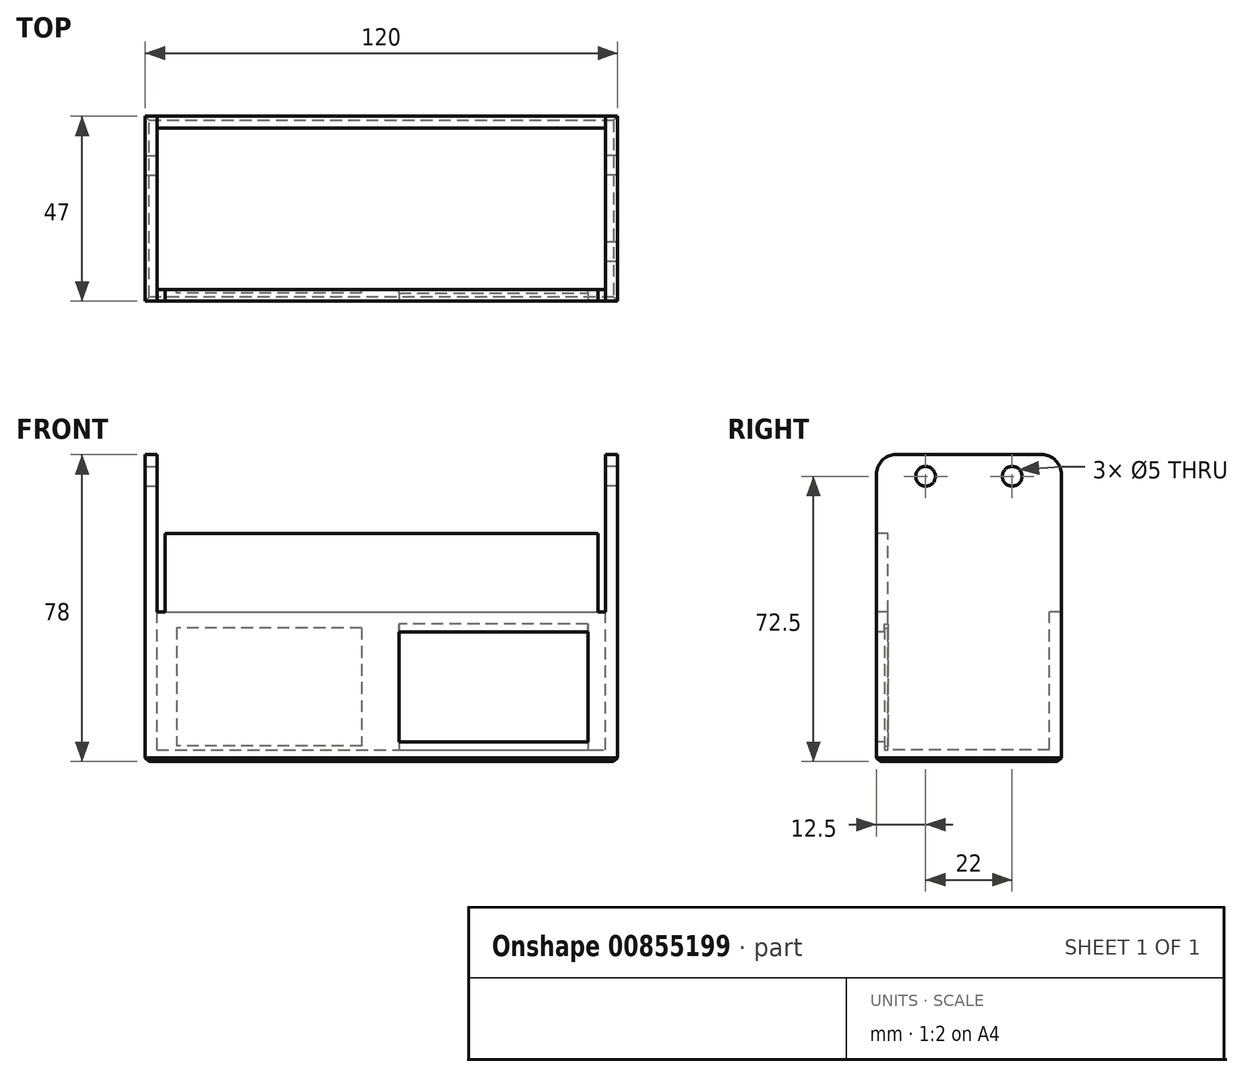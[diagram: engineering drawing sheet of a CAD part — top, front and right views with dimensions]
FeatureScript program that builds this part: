
annotation { "Feature Type Name" : "Feature", "Feature Type Description" : "" }
export const myFeature = defineFeature(function(context is Context, id is Id, definition is map)
    precondition{}
    {
        {
            assignVariable(context, id + "F0", {"name" : "wall", "anyValue" : 3});
        }
        {
            assignVariable(context, id + "F1", {"name" : "width", "anyValue" : 114});
        }
        {
            var Q0;
            Q0=qCreatedBy(makeId("Right.planeOp"),FACE);
            var sketch = newSketch(context, id + "F2", { "sketchPlane" : qUnion([Q0])});
            skLineSegment(sketch, "E0.bottom", {"start": v(17.5, 40) * mm, "end": v(-19.5, 40) * mm});
            skLineSegment(sketch, "E0.top", {"start": v(22.5, -38) * mm, "end": v(-24.5, -38) * mm});
            skLineSegment(sketch, "E0.left", {"start": v(22.5, 35) * mm, "end": v(22.5, -38) * mm});
            skLineSegment(sketch, "E0.right", {"start": v(-24.5, 35) * mm, "end": v(-24.5, -38) * mm});
            skCircle(sketch, "E1", {"center": v(10, 34.5) * mm, "radius": 2.5 * mm});
            skCircle(sketch, "E2", {"center": v(-12, 34.5) * mm, "radius": 2.5 * mm});
            skPoint(sketch, "E3.visualSharp", {"position": v(-24.5, 40) * mm});
            skArc(sketch, "E3.filletArc", {"start": v(-19.5, 40) * mm, "mid": v(-23.04, 38.54) * mm, "end": v(-24.5, 35) * mm});
            skPoint(sketch, "E4.visualSharp", {"position": v(22.5, 40) * mm});
            skArc(sketch, "E4.filletArc", {"start": v(22.5, 35) * mm, "mid": v(21.04, 38.54) * mm, "end": v(17.5, 40) * mm});
            skSolve(sketch);
        }
        {
            var Q0;
            Q0=qSketchRegion(id+"F2",true);
            extrude(context, id + "F3", {"entities" : qUnion([Q0]), "depth" : (getVariable(context, 'wall')) * mm, "offsetDistance" : 25 * mm});
        }
        {
            var Q0;
            Q0=qCreatedBy(makeId("Right.planeOp"),FACE);
            var sketch = newSketch(context, id + "F4", { "sketchPlane" : qUnion([Q0])});
            skLineSegment(sketch, "E5.bottom", {"start": v(22.5, -38) * mm, "end": v(-24.5, -38) * mm});
            skLineSegment(sketch, "E5.top", {"start": v(22.5, -35) * mm, "end": v(-24.5, -35) * mm});
            skLineSegment(sketch, "E5.left", {"start": v(22.5, -38) * mm, "end": v(22.5, -35) * mm});
            skLineSegment(sketch, "E5.right", {"start": v(-24.5, -38) * mm, "end": v(-24.5, -35) * mm});
            skLineSegment(sketch, "E6.bottom", {"start": v(-24.5, -38) * mm, "end": v(-21.5, -38) * mm});
            skLineSegment(sketch, "E6.top", {"start": v(-24.5, 0) * mm, "end": v(-21.5, 0) * mm});
            skLineSegment(sketch, "E6.left", {"start": v(-24.5, -38) * mm, "end": v(-24.5, 0) * mm});
            skLineSegment(sketch, "E6.right", {"start": v(-21.5, -38) * mm, "end": v(-21.5, 0) * mm});
            skLineSegment(sketch, "E7.bottom", {"start": v(22.5, -38) * mm, "end": v(19.5, -38) * mm});
            skLineSegment(sketch, "E7.top", {"start": v(22.5, 0) * mm, "end": v(19.5, 0) * mm});
            skLineSegment(sketch, "E7.left", {"start": v(22.5, -38) * mm, "end": v(22.5, 0) * mm});
            skLineSegment(sketch, "E7.right", {"start": v(19.5, -38) * mm, "end": v(19.5, 0) * mm});
            skSolve(sketch);
        }
        {
            var Q0;
            {var subQ0=sQuery(id+"F4.wireOp",EDGE,"E5.right");var subQ1=sQuery(id+"F4.wireOp",EDGE,"E5.bottom");var subQ9=sQuery(id+"F4.wireOp",EDGE,"E7.right");var subQ10=makeQuery(id+"F4.imprint","INTERSECT",VERTEX,{"derivedFrom":[subQ1,subQ9]});var subQ14=sQuery(id+"F4.wireOp",EDGE,"E5.left");var subQ16=sQuery(id+"F4.wireOp",EDGE,"E7.top");var subQ17=sQuery(id+"F4.wireOp",EDGE,"E6.top");Q0=qUnion([makeQuery(id+"F4.imprint","IMPRINT",FACE,{"disambiguationData":[TD([[makeQuery(id+"F4.imprint","IMPRINT",EDGE,{"derivedFrom":subQ17}),-1.0]])]}),makeQuery(id+"F4.imprint","IMPRINT",FACE,{"disambiguationData":[TD([[makeQuery(id+"F4.imprint","IMPRINT",EDGE,{"derivedFrom":subQ14}),1.0]])]}),makeQuery(id+"F4.imprint","IMPRINT",FACE,{"disambiguationData":[TD([[makeQuery(id+"F4.imprint","IMPRINT",EDGE,{"derivedFrom":subQ16}),1.0]])]}),makeQuery(id+"F4.imprint","IMPRINT",FACE,{"disambiguationData":[TD([[makeQuery(id+"F4.imprint","IMPRINT",EDGE,{"disambiguationData":[TD([[subQ10,-1.0]])],"derivedFrom":subQ1}),-1.0]])]}),makeQuery(id+"F4.imprint","IMPRINT",FACE,{"disambiguationData":[TD([[makeQuery(id+"F4.imprint","IMPRINT",EDGE,{"derivedFrom":subQ0}),-1.0]])]})]);}
            extrude(context, id + "F5", {"entities" : qUnion([Q0]), "operationType" : NewBodyOperationType.ADD, "oppositeDirection" : true, "depth" : (getVariable(context, 'width')) * mm, "offsetDistance" : 25 * mm});
        }
        {
            var Q0;
            Q0=makeQuery(id+"F5.opExtrude","CAP_FACE",FACE,{"disambiguationData":[OSD([sQuery(id+"F4.wireOp",EDGE,"E5.bottom"),sQuery(id+"F4.wireOp",EDGE,"E5.top"),sQuery(id+"F4.wireOp",EDGE,"E5.left"),sQuery(id+"F4.wireOp",EDGE,"E5.right"),sQuery(id+"F4.wireOp",EDGE,"E6.top"),sQuery(id+"F4.wireOp",EDGE,"E6.left"),sQuery(id+"F4.wireOp",EDGE,"E6.right"),sQuery(id+"F4.wireOp",EDGE,"E7.top"),sQuery(id+"F4.wireOp",EDGE,"E7.left"),sQuery(id+"F4.wireOp",EDGE,"E7.right")])],"isStart":false});
            var sketch = newSketch(context, id + "F6", { "sketchPlane" : qUnion([Q0])});
            skLineSegment(sketch, "E8.bottom", {"start": v(19.5, 40) * mm, "end": v(-17.5, 40) * mm});
            skLineSegment(sketch, "E8.top", {"start": v(24.5, -38) * mm, "end": v(-22.5, -38) * mm});
            skLineSegment(sketch, "E8.left", {"start": v(24.5, 35) * mm, "end": v(24.5, -38) * mm});
            skLineSegment(sketch, "E8.right", {"start": v(-22.5, 35) * mm, "end": v(-22.5, -38) * mm});
            skCircle(sketch, "E9", {"center": v(-10, 34.5) * mm, "radius": 2.5 * mm});
            skPoint(sketch, "E10.visualSharp", {"position": v(-22.5, 40) * mm});
            skArc(sketch, "E10.filletArc", {"start": v(-17.5, 40) * mm, "mid": v(-21.04, 38.54) * mm, "end": v(-22.5, 35) * mm});
            skPoint(sketch, "E11.visualSharp", {"position": v(24.5, 40) * mm});
            skArc(sketch, "E11.filletArc", {"start": v(24.5, 35) * mm, "mid": v(23.04, 38.54) * mm, "end": v(19.5, 40) * mm});
            skSolve(sketch);
        }
        {
            var Q0;
            Q0=qSketchRegion(id+"F6",true);
            extrude(context, id + "F7", {"entities" : qUnion([Q0]), "operationType" : NewBodyOperationType.ADD, "depth" : (getVariable(context, 'wall')) * mm, "offsetDistance" : 25 * mm});
        }
        {
            var Q0;
            Q0=makeQuery(id+"F7.boolean.opBoolean","MERGE",FACE,{"derivedFrom":[makeQuery(id+"F5.boolean.opBoolean","MERGE",FACE,{"derivedFrom":[makeQuery(id+"F3.opExtrude","SWEPT_FACE",FACE,{"disambiguationData":[OSD([sQuery(id+"F2.wireOp",EDGE,"E0.right")])]}),makeQuery(id+"F5.opExtrude","SWEPT_FACE",FACE,{"disambiguationData":[OSD([sQuery(id+"F4.wireOp",EDGE,"E5.right"),sQuery(id+"F4.wireOp",EDGE,"E6.left")])]})]}),makeQuery(id+"F7.opExtrude","SWEPT_FACE",FACE,{"disambiguationData":[OSD([sQuery(id+"F6.wireOp",EDGE,"E8.left")])]})]});
            var sketch = newSketch(context, id + "F8", { "sketchPlane" : qUnion([Q0])});
            skLineSegment(sketch, "E12.bottom", {"start": v(-112, 0) * mm, "end": v(-2, 0) * mm});
            skLineSegment(sketch, "E12.top", {"start": v(-112, 20) * mm, "end": v(-2, 20) * mm});
            skLineSegment(sketch, "E12.left", {"start": v(-112, 0) * mm, "end": v(-112, 20) * mm});
            skLineSegment(sketch, "E12.right", {"start": v(-2, 0) * mm, "end": v(-2, 20) * mm});
            skSolve(sketch);
        }
        {
            var Q0;
            Q0=qSketchRegion(id+"F8",true);
            extrude(context, id + "F9", {"entities" : qUnion([Q0]), "operationType" : NewBodyOperationType.ADD, "oppositeDirection" : true, "depth" : (getVariable(context, 'wall')) * mm, "offsetDistance" : 25 * mm});
        }
        {
            var Q0;
            {var subQ2=sQuery(id+"F8.wireOp",EDGE,"E12.bottom");Q0=makeQuery(id+"F8.imprint","IMPRINT",FACE,{"disambiguationData":[TD([[makeQuery(id+"F8.imprint","IMPRINT",EDGE,{"derivedFrom":subQ2}),-1.0]])]});}
            var sketch = newSketch(context, id + "F10", { "sketchPlane" : qUnion([Q0])});
            skLineSegment(sketch, "E13.bottom", {"start": v(-109, -6) * mm, "end": v(-62, -6) * mm});
            skLineSegment(sketch, "E13.top", {"start": v(-109, -32) * mm, "end": v(-62, -32) * mm});
            skLineSegment(sketch, "E13.left", {"start": v(-109, -6) * mm, "end": v(-109, -32) * mm});
            skLineSegment(sketch, "E13.right", {"start": v(-62, -6) * mm, "end": v(-62, -32) * mm});
            skLineSegment(sketch, "E14.bottom", {"start": v(-52.5, -5) * mm, "end": v(-4.5, -5) * mm});
            skLineSegment(sketch, "E14.top", {"start": v(-52.5, -33) * mm, "end": v(-4.5, -33) * mm});
            skLineSegment(sketch, "E14.left", {"start": v(-52.5, -5) * mm, "end": v(-52.5, -33) * mm});
            skLineSegment(sketch, "E14.right", {"start": v(-4.5, -5) * mm, "end": v(-4.5, -33) * mm});
            skLineSegment(sketch, "E15", {"start": v(-57, 0) * mm, "end": v(-57, -48.8) * mm, "construction": true});
            skLineSegment(sketch, "E16", {"start": v(-121.46, -19) * mm, "end": v(11.47, -19) * mm, "construction": true});
            skSolve(sketch);
        }
        {
            var Q0;
            Q0=qSketchRegion(id+"F10",true);
            extrude(context, id + "F11", {"entities" : qUnion([Q0]), "operationType" : NewBodyOperationType.REMOVE, "endBound" : BoundingType.UP_TO_NEXT, "oppositeDirection" : true, "depth" : 25 * mm, "offsetDistance" : 25 * mm});
        }
        {
            var Q0;
            Q0=makeQuery(id+"F7.boolean.opBoolean","MERGE",FACE,{"derivedFrom":[makeQuery(id+"F5.boolean.opBoolean","MERGE",FACE,{"derivedFrom":[makeQuery(id+"F3.opExtrude","SWEPT_FACE",FACE,{"disambiguationData":[OSD([sQuery(id+"F2.wireOp",EDGE,"E0.top")])]}),makeQuery(id+"F5.opExtrude","SWEPT_FACE",FACE,{"disambiguationData":[OSD([sQuery(id+"F4.wireOp",EDGE,"E5.bottom")])]})]}),makeQuery(id+"F7.opExtrude","SWEPT_FACE",FACE,{"disambiguationData":[OSD([sQuery(id+"F6.wireOp",EDGE,"E8.top")])]})]});
            chamfer(context, id + "F12", {"entities" : qUnion([Q0]), "width" : 1 * mm, "tangentPropagation" : true});
        }
        {
            assignVariable(context, id + "F13", {"name" : "InsertClipD", "anyValue" : 1});
        }
        {
            var Q0;
            Q0=makeQuery(id+"F9.boolean.opBoolean","MERGE",FACE,{"derivedFrom":[makeQuery(id+"F5.opExtrude","SWEPT_FACE",FACE,{"disambiguationData":[OSD([sQuery(id+"F4.wireOp",EDGE,"E6.right")])]}),makeQuery(id+"F9.opExtrude","CAP_FACE",FACE,{"disambiguationData":[OSD([sQuery(id+"F8.wireOp",EDGE,"E12.bottom"),sQuery(id+"F8.wireOp",EDGE,"E12.top"),sQuery(id+"F8.wireOp",EDGE,"E12.left"),sQuery(id+"F8.wireOp",EDGE,"E12.right")])],"isStart":false})]});
            var sketch = newSketch(context, id + "F14", { "sketchPlane" : qUnion([Q0])});
            skLineSegment(sketch, "E17.bottom", {"start": v(4.5, -5) * mm, "end": v(52.5, -5) * mm});
            skLineSegment(sketch, "E17.top", {"start": v(4.5, -3) * mm, "end": v(52.5, -3) * mm});
            skLineSegment(sketch, "E17.left", {"start": v(4.5, -5) * mm, "end": v(4.5, -3) * mm});
            skLineSegment(sketch, "E17.right", {"start": v(52.5, -5) * mm, "end": v(52.5, -3) * mm});
            skLineSegment(sketch, "E18.bottom", {"start": v(4.5, -33) * mm, "end": v(52.5, -33) * mm});
            skLineSegment(sketch, "E18.top", {"start": v(4.5, -35) * mm, "end": v(52.5, -35) * mm});
            skLineSegment(sketch, "E18.left", {"start": v(4.5, -33) * mm, "end": v(4.5, -35) * mm});
            skLineSegment(sketch, "E18.right", {"start": v(52.5, -33) * mm, "end": v(52.5, -35) * mm});
            skLineSegment(sketch, "E19.bottom", {"start": v(62, -4) * mm, "end": v(109, -4) * mm});
            skLineSegment(sketch, "E19.top", {"start": v(62, -6) * mm, "end": v(109, -6) * mm});
            skLineSegment(sketch, "E19.left", {"start": v(62, -4) * mm, "end": v(62, -6) * mm});
            skLineSegment(sketch, "E19.right", {"start": v(109, -4) * mm, "end": v(109, -6) * mm});
            skLineSegment(sketch, "E20.bottom", {"start": v(62, -34) * mm, "end": v(109, -34) * mm});
            skLineSegment(sketch, "E20.top", {"start": v(62, -32) * mm, "end": v(109, -32) * mm});
            skLineSegment(sketch, "E20.left", {"start": v(62, -34) * mm, "end": v(62, -32) * mm});
            skLineSegment(sketch, "E20.right", {"start": v(109, -34) * mm, "end": v(109, -32) * mm});
            skSolve(sketch);
        }
        {
            var Q0;
            Q0=makeQuery(id+"F14.imprint","IMPRINT",FACE,{"disambiguationData":[TD([[makeQuery(id+"F14.imprint","IMPRINT",EDGE,{"derivedFrom":sQuery(id+"F14.wireOp",EDGE,"E18.bottom")}),1.0]])]});
            var Q1;
            Q1=makeQuery(id+"F14.imprint","IMPRINT",FACE,{"disambiguationData":[TD([[makeQuery(id+"F14.imprint","IMPRINT",EDGE,{"derivedFrom":sQuery(id+"F14.wireOp",EDGE,"E20.bottom")}),1.0]])]});
            var Q2;
            Q2=makeQuery(id+"F14.imprint","IMPRINT",FACE,{"disambiguationData":[TD([[makeQuery(id+"F14.imprint","IMPRINT",EDGE,{"derivedFrom":sQuery(id+"F14.wireOp",EDGE,"E19.bottom")}),-1.0]])]});
            var Q3;
            Q3=makeQuery(id+"F14.imprint","IMPRINT",FACE,{"disambiguationData":[TD([[makeQuery(id+"F14.imprint","IMPRINT",EDGE,{"derivedFrom":sQuery(id+"F14.wireOp",EDGE,"E17.bottom")}),-1.0]])]});
            extrude(context, id + "F15", {"entities" : qUnion([Q0, Q1, Q2, Q3]), "operationType" : NewBodyOperationType.REMOVE, "oppositeDirection" : true, "depth" : (getVariable(context, 'InsertClipD')) * mm, "offsetDistance" : 25 * mm});
        }
        {
            var Q0;
            Q0=makeQuery(id+"F11.boolean.opBoolean","COPY",FACE,{"derivedFrom":makeQuery(id+"F11.opExtrude","SWEPT_FACE",FACE,{"disambiguationData":[OSD([sQuery(id+"F10.wireOp",EDGE,"E13.top")])]})});
            extrude(context, id + "F16", {"entities" : qUnion([Q0]), "operationType" : NewBodyOperationType.ADD, "depth" : 26 * mm, "offsetDistance" : 25 * mm});
        }
    });
